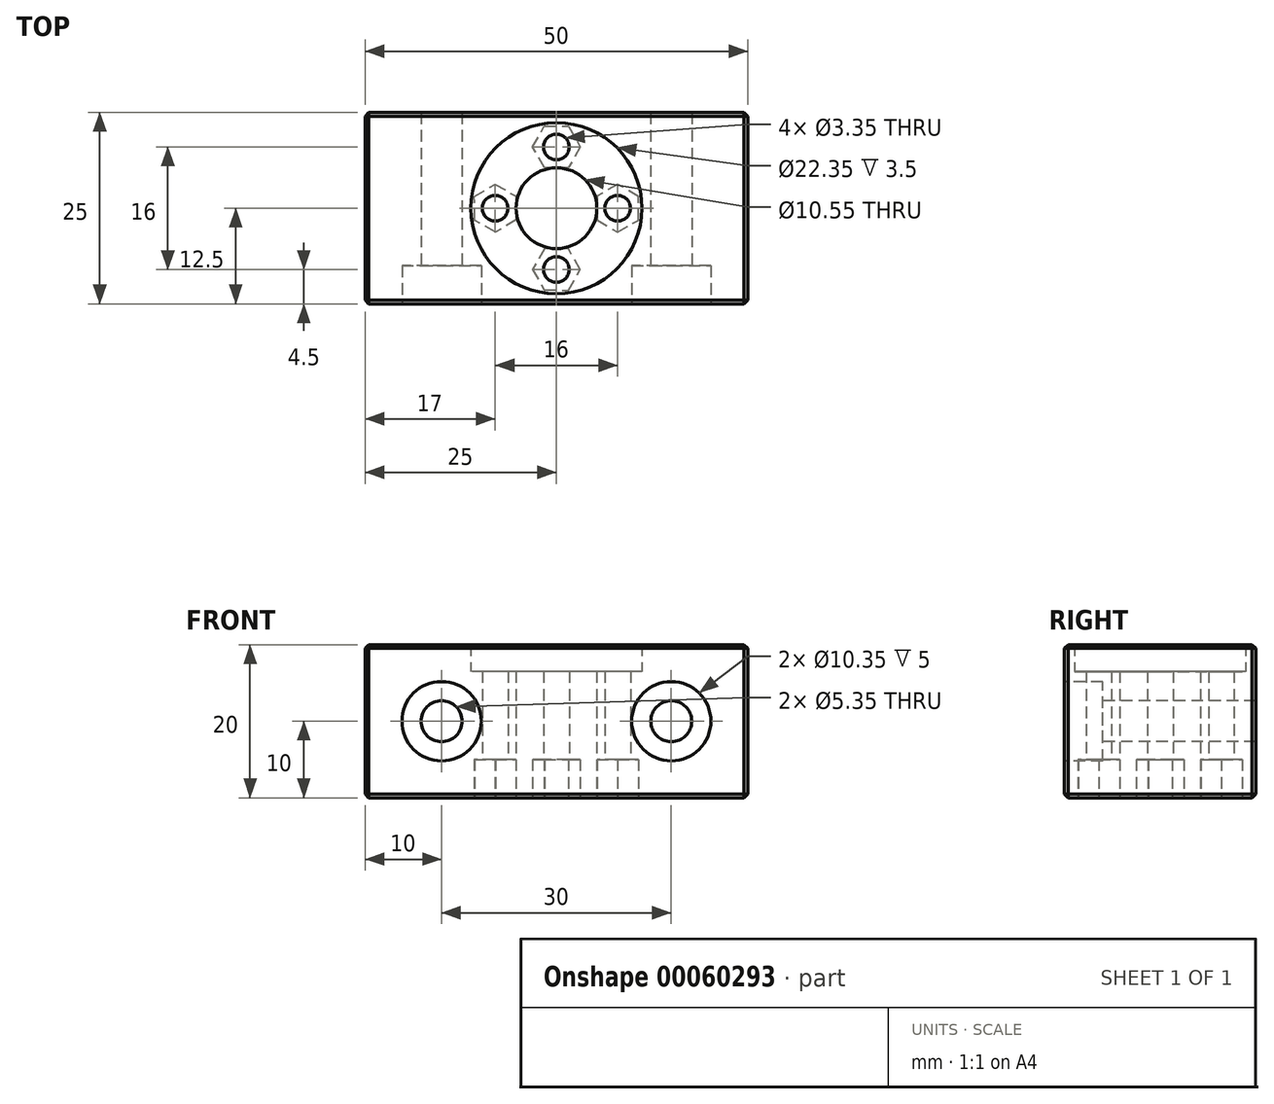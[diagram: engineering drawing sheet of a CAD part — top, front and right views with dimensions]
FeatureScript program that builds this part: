
annotation { "Feature Type Name" : "Feature", "Feature Type Description" : "" }
export const myFeature = defineFeature(function(context is Context, id is Id, definition is map)
    precondition{}
    {
        {
            var Q0;
            Q0=qCreatedBy(makeId("Top.planeOp"),FACE);
            var sketch = newSketch(context, id + "F0", { "sketchPlane" : qUnion([Q0])});
            skLineSegment(sketch, "E0.bottom", {"start": v(-25, 12.5) * mm, "end": v(25, 12.5) * mm});
            skLineSegment(sketch, "E0.top", {"start": v(-25, -12.5) * mm, "end": v(25, -12.5) * mm});
            skLineSegment(sketch, "E0.left", {"start": v(-25, 12.5) * mm, "end": v(-25, -12.5) * mm});
            skLineSegment(sketch, "E0.right", {"start": v(25, 12.5) * mm, "end": v(25, -12.5) * mm});
            skLineSegment(sketch, "E1", {"start": v(-25, 0) * mm, "end": v(25, 0) * mm});
            skLineSegment(sketch, "E2", {"start": v(0, 12.5) * mm, "end": v(0, -12.5) * mm});
            skCircle(sketch, "E3", {"center": v(0, 0) * mm, "radius": 5.28 * mm});
            skCircle(sketch, "E4", {"center": v(0, 0) * mm, "radius": 8 * mm});
            skCircle(sketch, "E5", {"center": v(0, 0) * mm, "radius": 11.18 * mm});
            skCircle(sketch, "E6", {"center": v(-8, 0) * mm, "radius": 1.68 * mm});
            skCircle(sketch, "E7.cCircle", {"center": v(-8, 0) * mm, "radius": 3.13 * mm, "construction": true});
            skLineSegment(sketch, "E7.0", {"start": v(-5.3, 1.58) * mm, "end": v(-5.29, -1.55) * mm});
            skLineSegment(sketch, "E7.1", {"start": v(-5.29, -1.55) * mm, "end": v(-7.98, -3.13) * mm});
            skLineSegment(sketch, "E7.2", {"start": v(-7.98, -3.13) * mm, "end": v(-10.7, -1.58) * mm});
            skLineSegment(sketch, "E7.3", {"start": v(-10.7, -1.58) * mm, "end": v(-10.71, 1.55) * mm});
            skLineSegment(sketch, "E7.4", {"start": v(-10.71, 1.55) * mm, "end": v(-8.02, 3.13) * mm});
            skLineSegment(sketch, "E7.5", {"start": v(-8.02, 3.13) * mm, "end": v(-5.3, 1.58) * mm});
            skCircle(sketch, "E8.MirrorC", {"center": v(8, 0) * mm, "radius": 3.13 * mm, "construction": true});
            skLineSegment(sketch, "E9.MirrorCS", {"start": v(10.71, 1.55) * mm, "end": v(8.02, 3.13) * mm});
            skLineSegment(sketch, "E10.MirrorCS", {"start": v(10.7, -1.58) * mm, "end": v(10.71, 1.55) * mm});
            skLineSegment(sketch, "E11.MirrorCS", {"start": v(5.29, -1.55) * mm, "end": v(7.98, -3.13) * mm});
            skLineSegment(sketch, "E12.MirrorCS", {"start": v(7.98, -3.13) * mm, "end": v(10.7, -1.58) * mm});
            skLineSegment(sketch, "E13.MirrorCS", {"start": v(8.02, 3.13) * mm, "end": v(5.3, 1.58) * mm});
            skLineSegment(sketch, "E14.MirrorCS", {"start": v(5.3, 1.58) * mm, "end": v(5.29, -1.55) * mm});
            skCircle(sketch, "E15.MirrorC", {"center": v(8, 0) * mm, "radius": 1.68 * mm});
            skLineSegment(sketch, "E16", {"start": v(0, -11.18) * mm, "end": v(0, 11.18) * mm});
            skLineSegment(sketch, "E17", {"start": v(0, 0) * mm, "end": v(-7.9, -7.9) * mm});
            skCircle(sketch, "E18.MirrorC", {"center": v(0, -8) * mm, "radius": 3.13 * mm, "construction": true});
            skLineSegment(sketch, "E19.MirrorCS", {"start": v(1.58, -5.3) * mm, "end": v(-1.55, -5.29) * mm});
            skLineSegment(sketch, "E20.MirrorCS", {"start": v(3.13, -8.02) * mm, "end": v(1.58, -5.3) * mm});
            skLineSegment(sketch, "E21.MirrorCS", {"start": v(-3.13, -7.98) * mm, "end": v(-1.58, -10.7) * mm});
            skCircle(sketch, "E22.MirrorC", {"center": v(0, -8) * mm, "radius": 1.68 * mm});
            skLineSegment(sketch, "E23.MirrorCS", {"start": v(-1.58, -10.7) * mm, "end": v(1.55, -10.71) * mm});
            skLineSegment(sketch, "E24.MirrorCS", {"start": v(-1.55, -5.29) * mm, "end": v(-3.13, -7.98) * mm});
            skLineSegment(sketch, "E25.MirrorCS", {"start": v(1.55, -10.71) * mm, "end": v(3.13, -8.02) * mm});
            skLineSegment(sketch, "E26.MirrorCS", {"start": v(3.13, 8.02) * mm, "end": v(1.58, 5.3) * mm});
            skLineSegment(sketch, "E27.MirrorCS", {"start": v(-1.55, 5.29) * mm, "end": v(-3.13, 7.98) * mm});
            skLineSegment(sketch, "E28.MirrorCS", {"start": v(1.55, 10.71) * mm, "end": v(3.13, 8.02) * mm});
            skLineSegment(sketch, "E29.MirrorCS", {"start": v(-3.13, 7.98) * mm, "end": v(-1.58, 10.7) * mm});
            skLineSegment(sketch, "E30.MirrorCS", {"start": v(1.58, 5.3) * mm, "end": v(-1.55, 5.29) * mm});
            skLineSegment(sketch, "E31.MirrorCS", {"start": v(-1.58, 10.7) * mm, "end": v(1.55, 10.71) * mm});
            skCircle(sketch, "E32.MirrorC", {"center": v(0, 8) * mm, "radius": 3.13 * mm, "construction": true});
            skCircle(sketch, "E33.MirrorC", {"center": v(0, 8) * mm, "radius": 1.68 * mm});
            skSolve(sketch);
        }
        {
            var Q0;
            Q0 = qSketchRegion(id + "F0", true);
            extrude(context, id + "F1", {"entities" : qUnion([Q0]), "depth" : 20 * mm});
        }
        {
            var Q0;
            {var subQ0=sQuery(id+"F0.wireOp",EDGE,"E5");var subQ1=sQuery(id+"F0.wireOp",EDGE,"E1");var subQ2=makeQuery(id+"F0.imprint","INTERSECT",VERTEX,{"disambiguationData":[OD(0.0)],"derivedFrom":[subQ1,subQ0]});Q0=makeQuery(id+"F0.imprint","IMPRINT",FACE,{"disambiguationData":[TD([[makeQuery(id+"F0.imprint","IMPRINT",EDGE,{"disambiguationData":[TD([[subQ2,-1.0]])],"derivedFrom":subQ1}),-1.0]])]});}
            var Q1;
            {var subQ0=sQuery(id+"F0.wireOp",EDGE,"E3");var subQ1=sQuery(id+"F0.wireOp",EDGE,"E1");var subQ2=makeQuery(id+"F0.imprint","INTERSECT",VERTEX,{"disambiguationData":[OD(1.0)],"derivedFrom":[subQ1,subQ0]});Q1=makeQuery(id+"F0.imprint","IMPRINT",FACE,{"disambiguationData":[TD([[makeQuery(id+"F0.imprint","IMPRINT",EDGE,{"disambiguationData":[TD([[subQ2,-1.0]])],"derivedFrom":subQ1}),-1.0]])]});}
            var Q2;
            {var subQ0=sQuery(id+"F0.wireOp",EDGE,"E3");var subQ1=sQuery(id+"F0.wireOp",EDGE,"E1");var subQ2=makeQuery(id+"F0.imprint","INTERSECT",VERTEX,{"disambiguationData":[OD(1.0)],"derivedFrom":[subQ1,subQ0]});Q2=makeQuery(id+"F0.imprint","IMPRINT",FACE,{"disambiguationData":[TD([[makeQuery(id+"F0.imprint","IMPRINT",EDGE,{"disambiguationData":[TD([[subQ2,-1.0]])],"derivedFrom":subQ1}),1.0]])]});}
            var Q3;
            {var subQ0=sQuery(id+"F0.wireOp",EDGE,"E5");var subQ1=sQuery(id+"F0.wireOp",EDGE,"E1");var subQ2=makeQuery(id+"F0.imprint","INTERSECT",VERTEX,{"disambiguationData":[OD(0.0)],"derivedFrom":[subQ1,subQ0]});Q3=makeQuery(id+"F0.imprint","IMPRINT",FACE,{"disambiguationData":[TD([[makeQuery(id+"F0.imprint","IMPRINT",EDGE,{"disambiguationData":[TD([[subQ2,-1.0]])],"derivedFrom":subQ1}),1.0]])]});}
            var Q4;
            {var subQ7=sQuery(id+"F0.wireOp",EDGE,"E7.0");var subQ8=sQuery(id+"F0.wireOp",EDGE,"E1");var subQ9=makeQuery(id+"F0.imprint","INTERSECT",VERTEX,{"derivedFrom":[subQ8,subQ7]});Q4=makeQuery(id+"F0.imprint","IMPRINT",FACE,{"disambiguationData":[TD([[makeQuery(id+"F0.imprint","IMPRINT",EDGE,{"disambiguationData":[TD([[subQ9,-1.0]])],"derivedFrom":subQ8}),-1.0]])]});}
            var Q5;
            {var subQ7=sQuery(id+"F0.wireOp",EDGE,"E1");var subQ9=sQuery(id+"F0.wireOp",EDGE,"E7.0");var subQ10=makeQuery(id+"F0.imprint","INTERSECT",VERTEX,{"derivedFrom":[subQ7,subQ9]});Q5=makeQuery(id+"F0.imprint","IMPRINT",FACE,{"disambiguationData":[TD([[makeQuery(id+"F0.imprint","IMPRINT",EDGE,{"disambiguationData":[TD([[subQ10,-1.0]])],"derivedFrom":subQ7}),1.0]])]});}
            var Q6;
            {var subQ3=sQuery(id+"F0.wireOp",EDGE,"E1");var subQ5=sQuery(id+"F0.wireOp",EDGE,"E6");var subQ6=makeQuery(id+"F0.imprint","INTERSECT",VERTEX,{"disambiguationData":[OD(1.0)],"derivedFrom":[subQ3,subQ5]});Q6=makeQuery(id+"F0.imprint","IMPRINT",FACE,{"disambiguationData":[TD([[makeQuery(id+"F0.imprint","IMPRINT",EDGE,{"disambiguationData":[TD([[subQ6,-1.0]])],"derivedFrom":subQ3}),1.0]])]});}
            var Q7;
            {var subQ0=sQuery(id+"F0.wireOp",EDGE,"E6");var subQ1=sQuery(id+"F0.wireOp",EDGE,"E1");var subQ2=makeQuery(id+"F0.imprint","INTERSECT",VERTEX,{"disambiguationData":[OD(1.0)],"derivedFrom":[subQ1,subQ0]});Q7=makeQuery(id+"F0.imprint","IMPRINT",FACE,{"disambiguationData":[TD([[makeQuery(id+"F0.imprint","IMPRINT",EDGE,{"disambiguationData":[TD([[subQ2,-1.0]])],"derivedFrom":subQ1}),-1.0]])]});}
            var Q8;
            {var subQ0=sQuery(id+"F0.wireOp",EDGE,"E7.4");Q8=makeQuery(id+"F0.imprint","IMPRINT",FACE,{"disambiguationData":[TD([[makeQuery(id+"F0.imprint","IMPRINT",EDGE,{"derivedFrom":subQ0}),-1.0]])]});}
            var Q9;
            {var subQ5=sQuery(id+"F0.wireOp",EDGE,"E7.2");Q9=makeQuery(id+"F0.imprint","IMPRINT",FACE,{"disambiguationData":[TD([[makeQuery(id+"F0.imprint","IMPRINT",EDGE,{"derivedFrom":subQ5}),-1.0]])]});}
            var Q10;
            {var subQ11=sQuery(id+"F0.wireOp",EDGE,"E21.MirrorCS");Q10=makeQuery(id+"F0.imprint","IMPRINT",FACE,{"disambiguationData":[TD([[makeQuery(id+"F0.imprint","IMPRINT",EDGE,{"derivedFrom":subQ11}),-1.0]])]});}
            var Q11;
            {var subQ0=sQuery(id+"F0.wireOp",EDGE,"E17");var subQ1=sQuery(id+"F0.wireOp",EDGE,"E3");var subQ2=makeQuery(id+"F0.imprint","INTERSECT",VERTEX,{"derivedFrom":[subQ1,subQ0]});Q11=makeQuery(id+"F0.imprint","IMPRINT",FACE,{"disambiguationData":[TD([[makeQuery(id+"F0.imprint","IMPRINT",EDGE,{"disambiguationData":[TD([[subQ2,-1.0]])],"derivedFrom":subQ1}),-1.0]])]});}
            var Q12;
            {var subQ1=sQuery(id+"F0.wireOp",EDGE,"E4");var subQ5=sQuery(id+"F0.wireOp",EDGE,"E24.MirrorCS");var subQ9=makeQuery(id+"F0.imprint","INTERSECT",VERTEX,{"derivedFrom":[subQ1,subQ5]});Q12=makeQuery(id+"F0.imprint","IMPRINT",FACE,{"disambiguationData":[TD([[makeQuery(id+"F0.imprint","IMPRINT",EDGE,{"disambiguationData":[TD([[subQ9,-1.0]])],"derivedFrom":subQ1}),1.0]])]});}
            var Q13;
            {var subQ5=sQuery(id+"F0.wireOp",EDGE,"E21.MirrorCS");Q13=makeQuery(id+"F0.imprint","IMPRINT",FACE,{"disambiguationData":[TD([[makeQuery(id+"F0.imprint","IMPRINT",EDGE,{"derivedFrom":subQ5}),1.0]])]});}
            var Q14;
            {var subQ5=sQuery(id+"F0.wireOp",EDGE,"E25.MirrorCS");Q14=makeQuery(id+"F0.imprint","IMPRINT",FACE,{"disambiguationData":[TD([[makeQuery(id+"F0.imprint","IMPRINT",EDGE,{"derivedFrom":subQ5}),1.0]])]});}
            var Q15;
            {var subQ5=sQuery(id+"F0.wireOp",EDGE,"E4");var subQ7=sQuery(id+"F0.wireOp",EDGE,"E22.MirrorC");var subQ9=makeQuery(id+"F0.imprint","INTERSECT",VERTEX,{"disambiguationData":[OD(1.0)],"derivedFrom":[subQ5,subQ7]});Q15=makeQuery(id+"F0.imprint","IMPRINT",FACE,{"disambiguationData":[TD([[makeQuery(id+"F0.imprint","IMPRINT",EDGE,{"disambiguationData":[TD([[subQ9,-1.0]])],"derivedFrom":subQ5}),1.0]])]});}
            var Q16;
            {var subQ0=sQuery(id+"F0.wireOp",EDGE,"E12.MirrorCS");Q16=makeQuery(id+"F0.imprint","IMPRINT",FACE,{"disambiguationData":[TD([[makeQuery(id+"F0.imprint","IMPRINT",EDGE,{"derivedFrom":subQ0}),-1.0]])]});}
            var Q17;
            {var subQ0=sQuery(id+"F0.wireOp",EDGE,"E9.MirrorCS");Q17=makeQuery(id+"F0.imprint","IMPRINT",FACE,{"disambiguationData":[TD([[makeQuery(id+"F0.imprint","IMPRINT",EDGE,{"derivedFrom":subQ0}),-1.0]])]});}
            var Q18;
            {var subQ0=sQuery(id+"F0.wireOp",EDGE,"E12.MirrorCS");Q18=makeQuery(id+"F0.imprint","IMPRINT",FACE,{"disambiguationData":[TD([[makeQuery(id+"F0.imprint","IMPRINT",EDGE,{"derivedFrom":subQ0}),1.0]])]});}
            var Q19;
            {var subQ1=sQuery(id+"F0.wireOp",EDGE,"E9.MirrorCS");Q19=makeQuery(id+"F0.imprint","IMPRINT",FACE,{"disambiguationData":[TD([[makeQuery(id+"F0.imprint","IMPRINT",EDGE,{"derivedFrom":subQ1}),1.0]])]});}
            var Q20;
            {var subQ0=sQuery(id+"F0.wireOp",EDGE,"E14.MirrorCS");var subQ3=sQuery(id+"F0.wireOp",EDGE,"E1");var subQ4=makeQuery(id+"F0.imprint","INTERSECT",VERTEX,{"derivedFrom":[subQ3,subQ0]});Q20=makeQuery(id+"F0.imprint","IMPRINT",FACE,{"disambiguationData":[TD([[makeQuery(id+"F0.imprint","IMPRINT",EDGE,{"disambiguationData":[TD([[subQ4,-1.0]])],"derivedFrom":subQ3}),1.0]])]});}
            var Q21;
            {var subQ0=sQuery(id+"F0.wireOp",EDGE,"E14.MirrorCS");var subQ5=sQuery(id+"F0.wireOp",EDGE,"E1");var subQ6=makeQuery(id+"F0.imprint","INTERSECT",VERTEX,{"derivedFrom":[subQ5,subQ0]});Q21=makeQuery(id+"F0.imprint","IMPRINT",FACE,{"disambiguationData":[TD([[makeQuery(id+"F0.imprint","IMPRINT",EDGE,{"disambiguationData":[TD([[subQ6,-1.0]])],"derivedFrom":subQ5}),-1.0]])]});}
            var Q22;
            {var subQ1=sQuery(id+"F0.wireOp",EDGE,"E26.MirrorCS");var subQ7=sQuery(id+"F0.wireOp",EDGE,"E4");var subQ8=makeQuery(id+"F0.imprint","INTERSECT",VERTEX,{"derivedFrom":[subQ7,subQ1]});Q22=makeQuery(id+"F0.imprint","IMPRINT",FACE,{"disambiguationData":[TD([[makeQuery(id+"F0.imprint","IMPRINT",EDGE,{"disambiguationData":[TD([[subQ8,-1.0]])],"derivedFrom":subQ7}),1.0]])]});}
            var Q23;
            {var subQ5=sQuery(id+"F0.wireOp",EDGE,"E33.MirrorC");var subQ7=sQuery(id+"F0.wireOp",EDGE,"E4");var subQ9=makeQuery(id+"F0.imprint","INTERSECT",VERTEX,{"disambiguationData":[OD(1.0)],"derivedFrom":[subQ7,subQ5]});Q23=makeQuery(id+"F0.imprint","IMPRINT",FACE,{"disambiguationData":[TD([[makeQuery(id+"F0.imprint","IMPRINT",EDGE,{"disambiguationData":[TD([[subQ9,-1.0]])],"derivedFrom":subQ7}),1.0]])]});}
            var Q24;
            {var subQ0=sQuery(id+"F0.wireOp",EDGE,"E29.MirrorCS");Q24=makeQuery(id+"F0.imprint","IMPRINT",FACE,{"disambiguationData":[TD([[makeQuery(id+"F0.imprint","IMPRINT",EDGE,{"derivedFrom":subQ0}),-1.0]])]});}
            var Q25;
            {var subQ0=sQuery(id+"F0.wireOp",EDGE,"E28.MirrorCS");Q25=makeQuery(id+"F0.imprint","IMPRINT",FACE,{"disambiguationData":[TD([[makeQuery(id+"F0.imprint","IMPRINT",EDGE,{"derivedFrom":subQ0}),-1.0]])]});}
            extrude(context, id + "F2", {"entities" : qUnion([Q0, Q1, Q2, Q3, Q4, Q5, Q6, Q7, Q8, Q9, Q10, Q11, Q12, Q13, Q14, Q15, Q16, Q17, Q18, Q19, Q20, Q21, Q22, Q23, Q24, Q25]), "operationType" : NewBodyOperationType.ADD, "depth" : 16.5 * mm});
        }
        {
            var Q0;
            {var subQ0=sQuery(id+"F0.wireOp",EDGE,"E6");var subQ1=sQuery(id+"F0.wireOp",EDGE,"E1");var subQ2=makeQuery(id+"F0.imprint","INTERSECT",VERTEX,{"disambiguationData":[OD(1.0)],"derivedFrom":[subQ1,subQ0]});Q0=makeQuery(id+"F0.imprint","IMPRINT",FACE,{"disambiguationData":[TD([[makeQuery(id+"F0.imprint","IMPRINT",EDGE,{"disambiguationData":[TD([[subQ2,-1.0]])],"derivedFrom":subQ1}),-1.0]])]});}
            var Q1;
            {var subQ3=sQuery(id+"F0.wireOp",EDGE,"E1");var subQ5=sQuery(id+"F0.wireOp",EDGE,"E6");var subQ6=makeQuery(id+"F0.imprint","INTERSECT",VERTEX,{"disambiguationData":[OD(1.0)],"derivedFrom":[subQ3,subQ5]});Q1=makeQuery(id+"F0.imprint","IMPRINT",FACE,{"disambiguationData":[TD([[makeQuery(id+"F0.imprint","IMPRINT",EDGE,{"disambiguationData":[TD([[subQ6,-1.0]])],"derivedFrom":subQ3}),1.0]])]});}
            var Q2;
            {var subQ0=sQuery(id+"F0.wireOp",EDGE,"E7.4");Q2=makeQuery(id+"F0.imprint","IMPRINT",FACE,{"disambiguationData":[TD([[makeQuery(id+"F0.imprint","IMPRINT",EDGE,{"derivedFrom":subQ0}),-1.0]])]});}
            var Q3;
            {var subQ5=sQuery(id+"F0.wireOp",EDGE,"E7.2");Q3=makeQuery(id+"F0.imprint","IMPRINT",FACE,{"disambiguationData":[TD([[makeQuery(id+"F0.imprint","IMPRINT",EDGE,{"derivedFrom":subQ5}),-1.0]])]});}
            var Q4;
            {var subQ1=sQuery(id+"F0.wireOp",EDGE,"E4");var subQ5=sQuery(id+"F0.wireOp",EDGE,"E24.MirrorCS");var subQ9=makeQuery(id+"F0.imprint","INTERSECT",VERTEX,{"derivedFrom":[subQ1,subQ5]});Q4=makeQuery(id+"F0.imprint","IMPRINT",FACE,{"disambiguationData":[TD([[makeQuery(id+"F0.imprint","IMPRINT",EDGE,{"disambiguationData":[TD([[subQ9,-1.0]])],"derivedFrom":subQ1}),1.0]])]});}
            var Q5;
            {var subQ5=sQuery(id+"F0.wireOp",EDGE,"E4");var subQ7=sQuery(id+"F0.wireOp",EDGE,"E22.MirrorC");var subQ9=makeQuery(id+"F0.imprint","INTERSECT",VERTEX,{"disambiguationData":[OD(1.0)],"derivedFrom":[subQ5,subQ7]});Q5=makeQuery(id+"F0.imprint","IMPRINT",FACE,{"disambiguationData":[TD([[makeQuery(id+"F0.imprint","IMPRINT",EDGE,{"disambiguationData":[TD([[subQ9,-1.0]])],"derivedFrom":subQ5}),1.0]])]});}
            var Q6;
            {var subQ5=sQuery(id+"F0.wireOp",EDGE,"E25.MirrorCS");Q6=makeQuery(id+"F0.imprint","IMPRINT",FACE,{"disambiguationData":[TD([[makeQuery(id+"F0.imprint","IMPRINT",EDGE,{"derivedFrom":subQ5}),1.0]])]});}
            var Q7;
            {var subQ5=sQuery(id+"F0.wireOp",EDGE,"E21.MirrorCS");Q7=makeQuery(id+"F0.imprint","IMPRINT",FACE,{"disambiguationData":[TD([[makeQuery(id+"F0.imprint","IMPRINT",EDGE,{"derivedFrom":subQ5}),1.0]])]});}
            var Q8;
            {var subQ0=sQuery(id+"F0.wireOp",EDGE,"E12.MirrorCS");Q8=makeQuery(id+"F0.imprint","IMPRINT",FACE,{"disambiguationData":[TD([[makeQuery(id+"F0.imprint","IMPRINT",EDGE,{"derivedFrom":subQ0}),1.0]])]});}
            var Q9;
            {var subQ0=sQuery(id+"F0.wireOp",EDGE,"E14.MirrorCS");var subQ5=sQuery(id+"F0.wireOp",EDGE,"E1");var subQ6=makeQuery(id+"F0.imprint","INTERSECT",VERTEX,{"derivedFrom":[subQ5,subQ0]});Q9=makeQuery(id+"F0.imprint","IMPRINT",FACE,{"disambiguationData":[TD([[makeQuery(id+"F0.imprint","IMPRINT",EDGE,{"disambiguationData":[TD([[subQ6,-1.0]])],"derivedFrom":subQ5}),-1.0]])]});}
            var Q10;
            {var subQ0=sQuery(id+"F0.wireOp",EDGE,"E14.MirrorCS");var subQ3=sQuery(id+"F0.wireOp",EDGE,"E1");var subQ4=makeQuery(id+"F0.imprint","INTERSECT",VERTEX,{"derivedFrom":[subQ3,subQ0]});Q10=makeQuery(id+"F0.imprint","IMPRINT",FACE,{"disambiguationData":[TD([[makeQuery(id+"F0.imprint","IMPRINT",EDGE,{"disambiguationData":[TD([[subQ4,-1.0]])],"derivedFrom":subQ3}),1.0]])]});}
            var Q11;
            {var subQ1=sQuery(id+"F0.wireOp",EDGE,"E9.MirrorCS");Q11=makeQuery(id+"F0.imprint","IMPRINT",FACE,{"disambiguationData":[TD([[makeQuery(id+"F0.imprint","IMPRINT",EDGE,{"derivedFrom":subQ1}),1.0]])]});}
            var Q12;
            {var subQ0=sQuery(id+"F0.wireOp",EDGE,"E28.MirrorCS");Q12=makeQuery(id+"F0.imprint","IMPRINT",FACE,{"disambiguationData":[TD([[makeQuery(id+"F0.imprint","IMPRINT",EDGE,{"derivedFrom":subQ0}),-1.0]])]});}
            var Q13;
            {var subQ1=sQuery(id+"F0.wireOp",EDGE,"E26.MirrorCS");var subQ7=sQuery(id+"F0.wireOp",EDGE,"E4");var subQ8=makeQuery(id+"F0.imprint","INTERSECT",VERTEX,{"derivedFrom":[subQ7,subQ1]});Q13=makeQuery(id+"F0.imprint","IMPRINT",FACE,{"disambiguationData":[TD([[makeQuery(id+"F0.imprint","IMPRINT",EDGE,{"disambiguationData":[TD([[subQ8,-1.0]])],"derivedFrom":subQ7}),1.0]])]});}
            var Q14;
            {var subQ5=sQuery(id+"F0.wireOp",EDGE,"E33.MirrorC");var subQ7=sQuery(id+"F0.wireOp",EDGE,"E4");var subQ9=makeQuery(id+"F0.imprint","INTERSECT",VERTEX,{"disambiguationData":[OD(1.0)],"derivedFrom":[subQ7,subQ5]});Q14=makeQuery(id+"F0.imprint","IMPRINT",FACE,{"disambiguationData":[TD([[makeQuery(id+"F0.imprint","IMPRINT",EDGE,{"disambiguationData":[TD([[subQ9,-1.0]])],"derivedFrom":subQ7}),1.0]])]});}
            var Q15;
            {var subQ0=sQuery(id+"F0.wireOp",EDGE,"E29.MirrorCS");Q15=makeQuery(id+"F0.imprint","IMPRINT",FACE,{"disambiguationData":[TD([[makeQuery(id+"F0.imprint","IMPRINT",EDGE,{"derivedFrom":subQ0}),-1.0]])]});}
            extrude(context, id + "F3", {"entities" : qUnion([Q0, Q1, Q2, Q3, Q4, Q5, Q6, Q7, Q8, Q9, Q10, Q11, Q12, Q13, Q14, Q15]), "operationType" : NewBodyOperationType.REMOVE, "depth" : 5 * mm});
        }
        {
            var Q0;
            Q0=makeQuery(id+"F1.opExtrude","SWEPT_FACE",FACE,{"disambiguationData":[OSD([sQuery(id+"F0.wireOp",EDGE,"E0.top")])]});
            var sketch = newSketch(context, id + "F4", { "sketchPlane" : qUnion([Q0])});
            skLineSegment(sketch, "E34", {"start": v(0, 20) * mm, "end": v(0, 0) * mm});
            skLineSegment(sketch, "E35", {"start": v(-25, 10) * mm, "end": v(25, 10) * mm});
            skLineSegment(sketch, "E36", {"start": v(-15, 20) * mm, "end": v(-15, 0) * mm});
            skLineSegment(sketch, "E37.MirrorCS", {"start": v(15, 20) * mm, "end": v(15, 0) * mm});
            skCircle(sketch, "E38", {"center": v(-15, 10) * mm, "radius": 2.67 * mm});
            skCircle(sketch, "E39", {"center": v(-15, 10) * mm, "radius": 5.17 * mm});
            skCircle(sketch, "E40.MirrorC", {"center": v(15, 10) * mm, "radius": 5.17 * mm});
            skCircle(sketch, "E41.MirrorC", {"center": v(15, 10) * mm, "radius": 2.67 * mm});
            skSolve(sketch);
        }
        {
            var Q0;
            Q0 = qSketchRegion(id + "F4", true);
            var Q1;
            {var subQ0=sQuery(id+"F4.wireOp",EDGE,"E38");var subQ1=sQuery(id+"F4.wireOp",EDGE,"E35");var subQ2=makeQuery(id+"F4.imprint","INTERSECT",VERTEX,{"disambiguationData":[OD(0.0)],"derivedFrom":[subQ1,subQ0]});Q1=makeQuery(id+"F4.imprint","IMPRINT",FACE,{"disambiguationData":[TD([[makeQuery(id+"F4.imprint","IMPRINT",EDGE,{"disambiguationData":[TD([[subQ2,-1.0]])],"derivedFrom":subQ1}),1.0]])]});}
            var Q2;
            {var subQ0=sQuery(id+"F4.wireOp",EDGE,"E38");var subQ1=sQuery(id+"F4.wireOp",EDGE,"E35");var subQ2=makeQuery(id+"F4.imprint","INTERSECT",VERTEX,{"disambiguationData":[OD(0.0)],"derivedFrom":[subQ1,subQ0]});Q2=makeQuery(id+"F4.imprint","IMPRINT",FACE,{"disambiguationData":[TD([[makeQuery(id+"F4.imprint","IMPRINT",EDGE,{"disambiguationData":[TD([[subQ2,-1.0]])],"derivedFrom":subQ1}),-1.0]])]});}
            var Q3;
            {var subQ0=sQuery(id+"F4.wireOp",EDGE,"E36");var subQ1=sQuery(id+"F4.wireOp",EDGE,"E35");var subQ2=makeQuery(id+"F4.imprint","INTERSECT",VERTEX,{"derivedFrom":[subQ1,subQ0]});Q3=makeQuery(id+"F4.imprint","IMPRINT",FACE,{"disambiguationData":[TD([[makeQuery(id+"F4.imprint","IMPRINT",EDGE,{"disambiguationData":[TD([[subQ2,-1.0]])],"derivedFrom":subQ1}),-1.0]])]});}
            var Q4;
            {var subQ0=sQuery(id+"F4.wireOp",EDGE,"E36");var subQ1=sQuery(id+"F4.wireOp",EDGE,"E35");var subQ2=makeQuery(id+"F4.imprint","INTERSECT",VERTEX,{"derivedFrom":[subQ1,subQ0]});Q4=makeQuery(id+"F4.imprint","IMPRINT",FACE,{"disambiguationData":[TD([[makeQuery(id+"F4.imprint","IMPRINT",EDGE,{"disambiguationData":[TD([[subQ2,-1.0]])],"derivedFrom":subQ1}),1.0]])]});}
            var Q5;
            {var subQ0=sQuery(id+"F4.wireOp",EDGE,"E41.MirrorC");var subQ1=sQuery(id+"F4.wireOp",EDGE,"E35");var subQ2=makeQuery(id+"F4.imprint","INTERSECT",VERTEX,{"disambiguationData":[OD(0.0)],"derivedFrom":[subQ1,subQ0]});Q5=makeQuery(id+"F4.imprint","IMPRINT",FACE,{"disambiguationData":[TD([[makeQuery(id+"F4.imprint","IMPRINT",EDGE,{"disambiguationData":[TD([[subQ2,-1.0]])],"derivedFrom":subQ1}),-1.0]])]});}
            var Q6;
            {var subQ0=sQuery(id+"F4.wireOp",EDGE,"E37.MirrorCS");var subQ1=sQuery(id+"F4.wireOp",EDGE,"E35");var subQ2=makeQuery(id+"F4.imprint","INTERSECT",VERTEX,{"derivedFrom":[subQ1,subQ0]});Q6=makeQuery(id+"F4.imprint","IMPRINT",FACE,{"disambiguationData":[TD([[makeQuery(id+"F4.imprint","IMPRINT",EDGE,{"disambiguationData":[TD([[subQ2,-1.0]])],"derivedFrom":subQ1}),-1.0]])]});}
            var Q7;
            {var subQ0=sQuery(id+"F4.wireOp",EDGE,"E37.MirrorCS");var subQ1=sQuery(id+"F4.wireOp",EDGE,"E35");var subQ2=makeQuery(id+"F4.imprint","INTERSECT",VERTEX,{"derivedFrom":[subQ1,subQ0]});Q7=makeQuery(id+"F4.imprint","IMPRINT",FACE,{"disambiguationData":[TD([[makeQuery(id+"F4.imprint","IMPRINT",EDGE,{"disambiguationData":[TD([[subQ2,-1.0]])],"derivedFrom":subQ1}),1.0]])]});}
            var Q8;
            {var subQ0=sQuery(id+"F4.wireOp",EDGE,"E41.MirrorC");var subQ1=sQuery(id+"F4.wireOp",EDGE,"E35");var subQ2=makeQuery(id+"F4.imprint","INTERSECT",VERTEX,{"disambiguationData":[OD(0.0)],"derivedFrom":[subQ1,subQ0]});Q8=makeQuery(id+"F4.imprint","IMPRINT",FACE,{"disambiguationData":[TD([[makeQuery(id+"F4.imprint","IMPRINT",EDGE,{"disambiguationData":[TD([[subQ2,-1.0]])],"derivedFrom":subQ1}),1.0]])]});}
            extrude(context, id + "F5", {"entities" : qUnion([Q0, Q1, Q2, Q3, Q4, Q5, Q6, Q7, Q8]), "operationType" : NewBodyOperationType.REMOVE, "oppositeDirection" : true, "depth" : 5 * mm});
        }
        {
            var Q0;
            {var subQ0=sQuery(id+"F4.wireOp",EDGE,"E38");var subQ1=sQuery(id+"F4.wireOp",EDGE,"E35");var subQ2=makeQuery(id+"F4.imprint","INTERSECT",VERTEX,{"disambiguationData":[OD(0.0)],"derivedFrom":[subQ1,subQ0]});Q0=makeQuery(id+"F4.imprint","IMPRINT",FACE,{"disambiguationData":[TD([[makeQuery(id+"F4.imprint","IMPRINT",EDGE,{"disambiguationData":[TD([[subQ2,-1.0]])],"derivedFrom":subQ1}),1.0]])]});}
            var Q1;
            {var subQ0=sQuery(id+"F4.wireOp",EDGE,"E36");var subQ1=sQuery(id+"F4.wireOp",EDGE,"E35");var subQ2=makeQuery(id+"F4.imprint","INTERSECT",VERTEX,{"derivedFrom":[subQ1,subQ0]});Q1=makeQuery(id+"F4.imprint","IMPRINT",FACE,{"disambiguationData":[TD([[makeQuery(id+"F4.imprint","IMPRINT",EDGE,{"disambiguationData":[TD([[subQ2,-1.0]])],"derivedFrom":subQ1}),1.0]])]});}
            var Q2;
            {var subQ0=sQuery(id+"F4.wireOp",EDGE,"E36");var subQ1=sQuery(id+"F4.wireOp",EDGE,"E35");var subQ2=makeQuery(id+"F4.imprint","INTERSECT",VERTEX,{"derivedFrom":[subQ1,subQ0]});Q2=makeQuery(id+"F4.imprint","IMPRINT",FACE,{"disambiguationData":[TD([[makeQuery(id+"F4.imprint","IMPRINT",EDGE,{"disambiguationData":[TD([[subQ2,-1.0]])],"derivedFrom":subQ1}),-1.0]])]});}
            var Q3;
            {var subQ0=sQuery(id+"F4.wireOp",EDGE,"E38");var subQ1=sQuery(id+"F4.wireOp",EDGE,"E35");var subQ2=makeQuery(id+"F4.imprint","INTERSECT",VERTEX,{"disambiguationData":[OD(0.0)],"derivedFrom":[subQ1,subQ0]});Q3=makeQuery(id+"F4.imprint","IMPRINT",FACE,{"disambiguationData":[TD([[makeQuery(id+"F4.imprint","IMPRINT",EDGE,{"disambiguationData":[TD([[subQ2,-1.0]])],"derivedFrom":subQ1}),-1.0]])]});}
            var Q4;
            {var subQ0=sQuery(id+"F4.wireOp",EDGE,"E41.MirrorC");var subQ1=sQuery(id+"F4.wireOp",EDGE,"E35");var subQ2=makeQuery(id+"F4.imprint","INTERSECT",VERTEX,{"disambiguationData":[OD(0.0)],"derivedFrom":[subQ1,subQ0]});Q4=makeQuery(id+"F4.imprint","IMPRINT",FACE,{"disambiguationData":[TD([[makeQuery(id+"F4.imprint","IMPRINT",EDGE,{"disambiguationData":[TD([[subQ2,-1.0]])],"derivedFrom":subQ1}),1.0]])]});}
            var Q5;
            {var subQ0=sQuery(id+"F4.wireOp",EDGE,"E37.MirrorCS");var subQ1=sQuery(id+"F4.wireOp",EDGE,"E35");var subQ2=makeQuery(id+"F4.imprint","INTERSECT",VERTEX,{"derivedFrom":[subQ1,subQ0]});Q5=makeQuery(id+"F4.imprint","IMPRINT",FACE,{"disambiguationData":[TD([[makeQuery(id+"F4.imprint","IMPRINT",EDGE,{"disambiguationData":[TD([[subQ2,-1.0]])],"derivedFrom":subQ1}),1.0]])]});}
            var Q6;
            {var subQ0=sQuery(id+"F4.wireOp",EDGE,"E37.MirrorCS");var subQ1=sQuery(id+"F4.wireOp",EDGE,"E35");var subQ2=makeQuery(id+"F4.imprint","INTERSECT",VERTEX,{"derivedFrom":[subQ1,subQ0]});Q6=makeQuery(id+"F4.imprint","IMPRINT",FACE,{"disambiguationData":[TD([[makeQuery(id+"F4.imprint","IMPRINT",EDGE,{"disambiguationData":[TD([[subQ2,-1.0]])],"derivedFrom":subQ1}),-1.0]])]});}
            var Q7;
            {var subQ0=sQuery(id+"F4.wireOp",EDGE,"E41.MirrorC");var subQ1=sQuery(id+"F4.wireOp",EDGE,"E35");var subQ2=makeQuery(id+"F4.imprint","INTERSECT",VERTEX,{"disambiguationData":[OD(0.0)],"derivedFrom":[subQ1,subQ0]});Q7=makeQuery(id+"F4.imprint","IMPRINT",FACE,{"disambiguationData":[TD([[makeQuery(id+"F4.imprint","IMPRINT",EDGE,{"disambiguationData":[TD([[subQ2,-1.0]])],"derivedFrom":subQ1}),-1.0]])]});}
            extrude(context, id + "F6", {"entities" : qUnion([Q0, Q1, Q2, Q3, Q4, Q5, Q6, Q7]), "operationType" : NewBodyOperationType.REMOVE, "oppositeDirection" : true, "depth" : 25 * mm});
        }
        {
            var Q0;
            Q0=makeQuery(id+"F1.opExtrude","CAP_EDGE",EDGE,{"disambiguationData":[OSD([sQuery(id+"F0.wireOp",EDGE,"E0.top")])],"isStart":false});
            var Q1;
            Q1=makeQuery(id+"F1.opExtrude","CAP_EDGE",EDGE,{"disambiguationData":[OSD([sQuery(id+"F0.wireOp",EDGE,"E0.right")])],"isStart":false});
            var Q2;
            Q2=makeQuery(id+"F1.opExtrude","CAP_EDGE",EDGE,{"disambiguationData":[OSD([sQuery(id+"F0.wireOp",EDGE,"E0.bottom")])],"isStart":false});
            var Q3;
            Q3=makeQuery(id+"F1.opExtrude","CAP_EDGE",EDGE,{"disambiguationData":[OSD([sQuery(id+"F0.wireOp",EDGE,"E0.left")])],"isStart":false});
            var Q4;
            Q4=makeQuery(id+"F1.opExtrude","SWEPT_EDGE",EDGE,{"disambiguationData":[OSD([sQuery(id+"F0.wireOp",EDGE,"E0.bottom"),sQuery(id+"F0.wireOp",EDGE,"E0.left")])]});
            var Q5;
            Q5=makeQuery(id+"F1.opExtrude","SWEPT_EDGE",EDGE,{"disambiguationData":[OSD([sQuery(id+"F0.wireOp",EDGE,"E0.top"),sQuery(id+"F0.wireOp",EDGE,"E0.left")])]});
            var Q6;
            Q6=makeQuery(id+"F1.opExtrude","CAP_EDGE",EDGE,{"disambiguationData":[OSD([sQuery(id+"F0.wireOp",EDGE,"E0.left")])],"isStart":true});
            var Q7;
            Q7=makeQuery(id+"F1.opExtrude","CAP_EDGE",EDGE,{"disambiguationData":[OSD([sQuery(id+"F0.wireOp",EDGE,"E0.bottom")])],"isStart":true});
            var Q8;
            Q8=makeQuery(id+"F1.opExtrude","CAP_EDGE",EDGE,{"disambiguationData":[OSD([sQuery(id+"F0.wireOp",EDGE,"E0.top")])],"isStart":true});
            var Q9;
            Q9=makeQuery(id+"F1.opExtrude","SWEPT_EDGE",EDGE,{"disambiguationData":[OSD([sQuery(id+"F0.wireOp",EDGE,"E0.top"),sQuery(id+"F0.wireOp",EDGE,"E0.right")])]});
            var Q10;
            Q10=makeQuery(id+"F1.opExtrude","CAP_EDGE",EDGE,{"disambiguationData":[OSD([sQuery(id+"F0.wireOp",EDGE,"E0.right")])],"isStart":true});
            var Q11;
            Q11=makeQuery(id+"F1.opExtrude","SWEPT_EDGE",EDGE,{"disambiguationData":[OSD([sQuery(id+"F0.wireOp",EDGE,"E0.bottom"),sQuery(id+"F0.wireOp",EDGE,"E0.right")])]});
            chamfer(context, id + "F7", {"entities" : qUnion([Q0, Q1, Q2, Q3, Q4, Q5, Q6, Q7, Q8, Q9, Q10, Q11]), "width" : 0.5 * mm, "tangentPropagation" : true});
        }
    });
